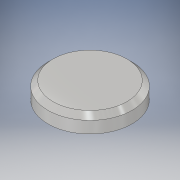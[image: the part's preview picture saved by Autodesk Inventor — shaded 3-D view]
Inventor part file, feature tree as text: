
AUTODESK INVENTOR PART (.ipt)
format: ipt  version: 2018 (Build 220112000, 112)  size: 105,984 bytes
history: native  units: in
note: dims shown in document units (in); Inventor stores cm internally (conversion verified against a paired STEP export)
features: extrude x1, chamfer x1, hole x1, sketch x1
ambient origin geometry x8: Origin, YZ Plane, XZ Plane, XY Plane, X Axis, Y Axis, Z Axis, Center Point
bodies: Solid1 (feature_tree)
feature tree (4):
  extrude  "Extrusion1"  Depth=0.3937in TaperAngle=0.0deg
  chamfer  "Chamfer1"  Distance=0.1181in Angle=45.0deg
  hole  "Hole1"  [1 undecoded]
  sketch  "Sketch1"  dims[d0=1.9685in d1=0.3937in d2=0.0in d3=0.1181in d4=0.0787in d5=45.0deg d6=0.3937in d7=0.3937in d8=0.3937in d9=0.2362in d10=0.1575in d11=0.0787in d12=90.0deg d13=0.1969in d14=0.0in]
note: 1 required parameter value undecoded (feature->parameter linkage not recoverable at this tier; creation-order binding heuristic only, values carry confidence <= 0.55)
